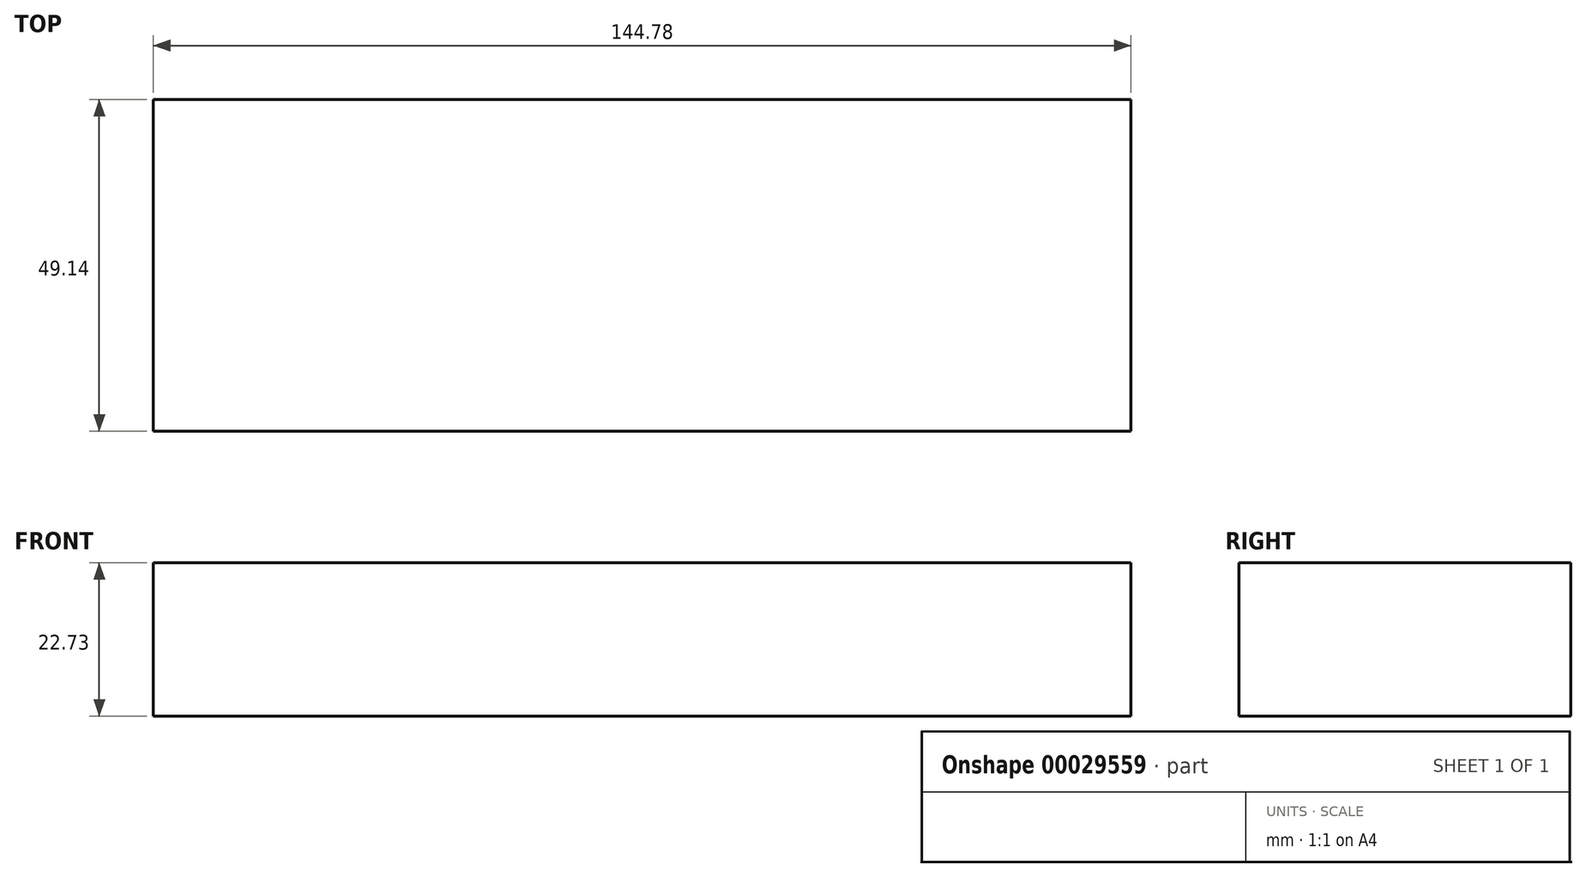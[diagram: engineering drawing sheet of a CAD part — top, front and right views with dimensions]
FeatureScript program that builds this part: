
annotation { "Feature Type Name" : "Feature", "Feature Type Description" : "" }
export const myFeature = defineFeature(function(context is Context, id is Id, definition is map)
    precondition{}
    {
        {
            var Q0;
            Q0=qCreatedBy(makeId("Top.planeOp"),FACE);
            var sketch = newSketch(context, id + "F0", { "sketchPlane" : qUnion([Q0])});
            skLineSegment(sketch, "E0.rect.bottom", {"start": v(72.4, 24.57) * mm, "end": v(-72.4, 24.57) * mm});
            skLineSegment(sketch, "E0.rect.top", {"start": v(72.4, -24.57) * mm, "end": v(-72.4, -24.57) * mm});
            skLineSegment(sketch, "E0.rect.left", {"start": v(72.4, 24.57) * mm, "end": v(72.4, -24.57) * mm});
            skLineSegment(sketch, "E0.rect.right", {"start": v(-72.4, 24.57) * mm, "end": v(-72.4, -24.57) * mm});
            skPoint(sketch, "E0.rect.middle", {"position": v(0, 0) * mm});
            skSolve(sketch);
        }
        {
            var Q0;
            Q0 = qSketchRegion(id + "F0", true);
            extrude(context, id + "F1", {"entities" : qUnion([Q0]), "depth" : 22.73 * mm});
        }
    });
